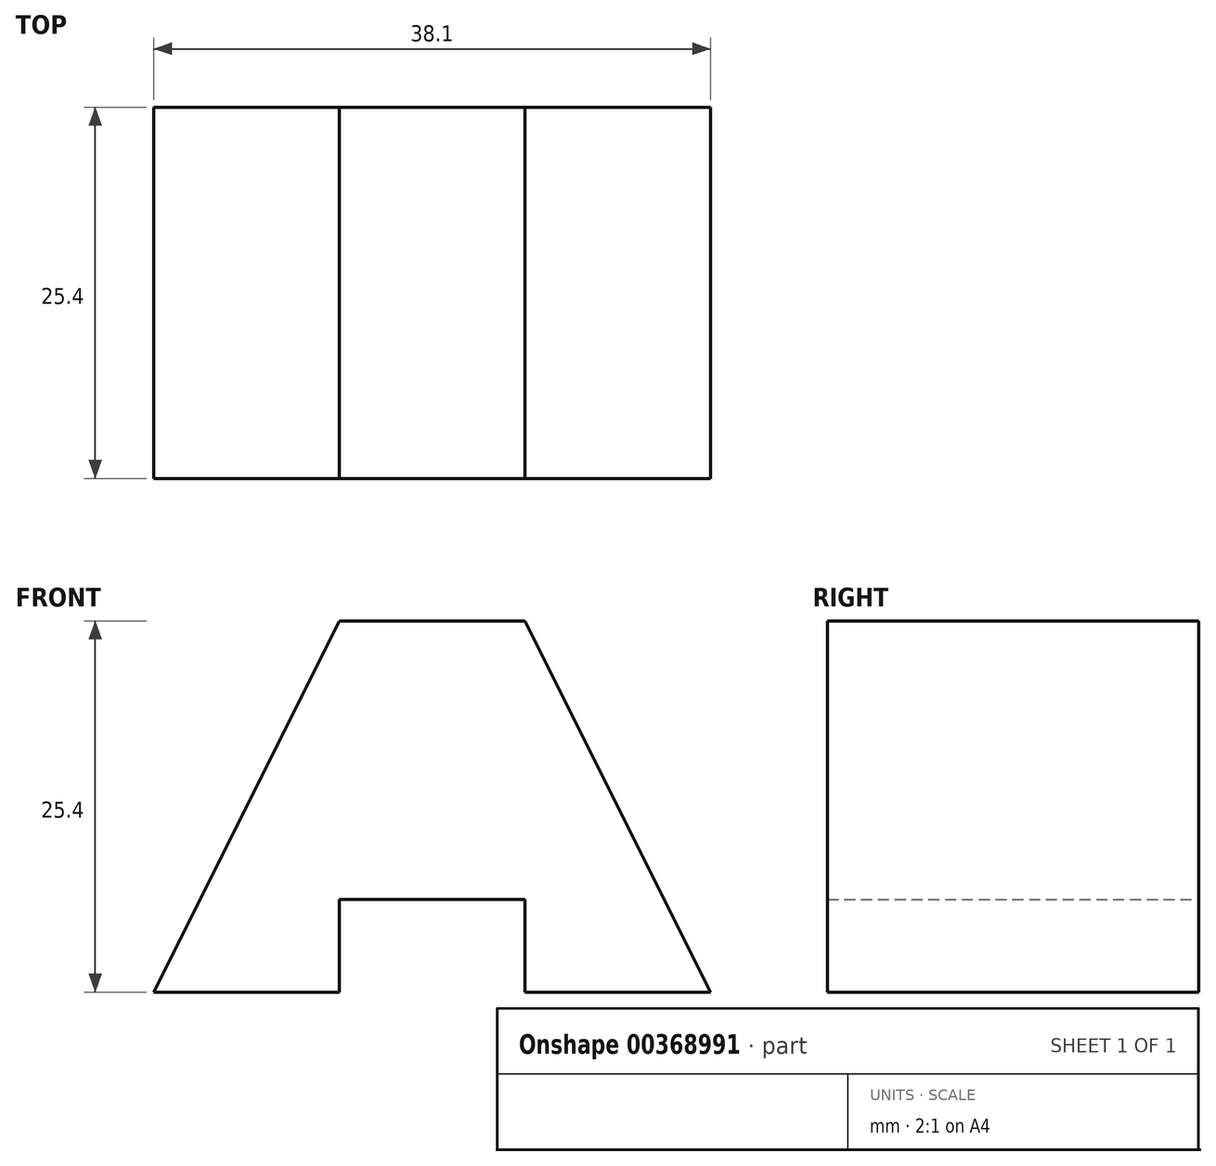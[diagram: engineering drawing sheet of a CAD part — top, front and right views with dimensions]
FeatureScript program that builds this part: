
annotation { "Feature Type Name" : "Feature", "Feature Type Description" : "" }
export const myFeature = defineFeature(function(context is Context, id is Id, definition is map)
    precondition{}
    {
        {
            var Q0;
            Q0=qCreatedBy(makeId("Front.planeOp"),FACE);
            var sketch = newSketch(context, id + "F0", { "sketchPlane" : qUnion([Q0])});
            skLineSegment(sketch, "E0", {"start": v(0, 0) * mm, "end": v(12.7, 0) * mm});
            skLineSegment(sketch, "E1", {"start": v(12.7, 0) * mm, "end": v(12.7, 6.35) * mm});
            skLineSegment(sketch, "E2", {"start": v(12.7, 6.35) * mm, "end": v(25.4, 6.35) * mm});
            skLineSegment(sketch, "E3", {"start": v(25.4, 6.35) * mm, "end": v(25.4, 0) * mm});
            skLineSegment(sketch, "E4", {"start": v(25.4, 0) * mm, "end": v(38.1, 0) * mm});
            skLineSegment(sketch, "E5", {"start": v(38.1, 0) * mm, "end": v(25.4, 25.4) * mm});
            skLineSegment(sketch, "E6", {"start": v(25.4, 25.4) * mm, "end": v(12.7, 25.4) * mm});
            skLineSegment(sketch, "E7", {"start": v(12.7, 25.4) * mm, "end": v(0, 0) * mm});
            skSolve(sketch);
        }
        {
            var Q0;
            Q0 = qSketchRegion(id + "F0", true);
            extrude(context, id + "F1", {"entities" : qUnion([Q0]), "depth" : 25.4 * mm});
        }
    });
